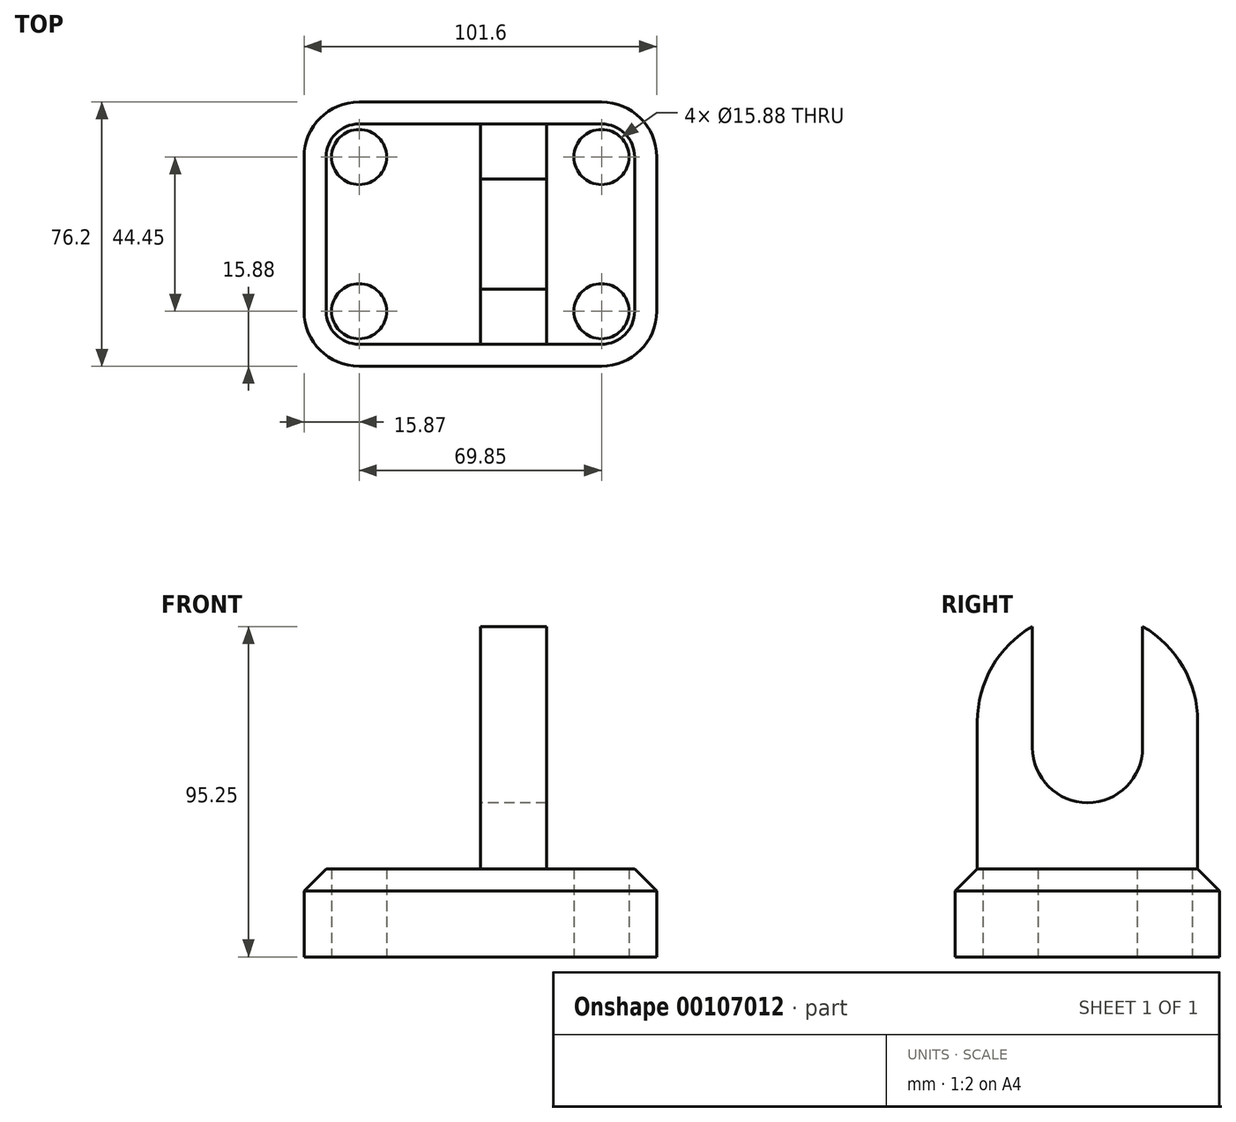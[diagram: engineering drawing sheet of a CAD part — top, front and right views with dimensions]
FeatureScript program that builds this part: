
annotation { "Feature Type Name" : "Feature", "Feature Type Description" : "" }
export const myFeature = defineFeature(function(context is Context, id is Id, definition is map)
    precondition{}
    {
        {
            var Q0;
            Q0=qCreatedBy(makeId("Top.planeOp"),FACE);
            var sketch = newSketch(context, id + "F0", { "sketchPlane" : qUnion([Q0])});
            skLineSegment(sketch, "E0.bottom", {"start": v(-44.56, 20.5) * mm, "end": v(57.04, 20.5) * mm});
            skLineSegment(sketch, "E0.top", {"start": v(-44.56, -55.7) * mm, "end": v(57.04, -55.7) * mm});
            skLineSegment(sketch, "E0.left", {"start": v(-44.56, 20.5) * mm, "end": v(-44.56, -55.7) * mm});
            skLineSegment(sketch, "E0.right", {"start": v(57.04, 20.5) * mm, "end": v(57.04, -55.7) * mm});
            skSolve(sketch);
        }
        {
            var Q0;
            Q0=makeQuery(id+"F0.imprint","IMPRINT",FACE,{"disambiguationData":[TD([[makeQuery(id+"F0.imprint","IMPRINT",EDGE,{"derivedFrom":sQuery(id+"F0.wireOp",EDGE,"E0.bottom")}),-1.0]])]});
            extrude(context, id + "F1", {"entities" : qUnion([Q0]), "depth" : 25.4 * mm});
        }
        {
            var Q0;
            Q0=makeQuery(id+"F1.opExtrude","SWEPT_EDGE",EDGE,{"disambiguationData":[OSD([sQuery(id+"F0.wireOp",EDGE,"E0.top"),sQuery(id+"F0.wireOp",EDGE,"E0.right")])]});
            fillet(context, id + "F2", {"entities" : qUnion([Q0]), "radius" : 15.88 * mm, "tangentPropagation" : true, "allowEdgeOverflow" : false});
        }
        {
            var Q0;
            Q0=makeQuery(id+"F1.opExtrude","SWEPT_EDGE",EDGE,{"disambiguationData":[OSD([sQuery(id+"F0.wireOp",EDGE,"E0.top"),sQuery(id+"F0.wireOp",EDGE,"E0.left")])]});
            fillet(context, id + "F3", {"entities" : qUnion([Q0]), "radius" : 15.88 * mm, "tangentPropagation" : true, "allowEdgeOverflow" : false});
        }
        {
            var Q0;
            Q0=makeQuery(id+"F1.opExtrude","SWEPT_EDGE",EDGE,{"disambiguationData":[OSD([sQuery(id+"F0.wireOp",EDGE,"E0.bottom"),sQuery(id+"F0.wireOp",EDGE,"E0.left")])]});
            fillet(context, id + "F4", {"entities" : qUnion([Q0]), "radius" : 15.88 * mm, "tangentPropagation" : true, "allowEdgeOverflow" : false});
        }
        {
            var Q0;
            Q0=makeQuery(id+"F1.opExtrude","SWEPT_EDGE",EDGE,{"disambiguationData":[OSD([sQuery(id+"F0.wireOp",EDGE,"E0.bottom"),sQuery(id+"F0.wireOp",EDGE,"E0.right")])]});
            fillet(context, id + "F5", {"entities" : qUnion([Q0]), "radius" : 15.88 * mm, "tangentPropagation" : true, "allowEdgeOverflow" : false});
        }
        {
            var Q0;
            Q0=makeQuery(id+"F1.opExtrude","CAP_FACE",FACE,{"disambiguationData":[OSD([sQuery(id+"F0.wireOp",EDGE,"E0.bottom"),sQuery(id+"F0.wireOp",EDGE,"E0.top"),sQuery(id+"F0.wireOp",EDGE,"E0.left"),sQuery(id+"F0.wireOp",EDGE,"E0.right")])],"isStart":true});
            var sketch = newSketch(context, id + "F6", { "sketchPlane" : qUnion([Q0])});
            skLineSegment(sketch, "E1.bottom", {"start": v(-44.56, -4.62) * mm, "end": v(-28.69, -4.62) * mm});
            skLineSegment(sketch, "E1.top", {"start": v(-44.56, -20.5) * mm, "end": v(-28.69, -20.5) * mm});
            skLineSegment(sketch, "E1.left", {"start": v(-44.56, -4.62) * mm, "end": v(-44.56, -20.5) * mm});
            skLineSegment(sketch, "E1.right", {"start": v(-28.69, -4.62) * mm, "end": v(-28.69, -20.5) * mm});
            skLineSegment(sketch, "E2.bottom", {"start": v(-44.56, 39.83) * mm, "end": v(-28.69, 39.83) * mm});
            skLineSegment(sketch, "E2.top", {"start": v(-44.56, 55.7) * mm, "end": v(-28.69, 55.7) * mm});
            skLineSegment(sketch, "E2.left", {"start": v(-44.56, 39.83) * mm, "end": v(-44.56, 55.7) * mm});
            skLineSegment(sketch, "E2.right", {"start": v(-28.69, 39.83) * mm, "end": v(-28.69, 55.7) * mm});
            skLineSegment(sketch, "E3.bottom", {"start": v(41.16, 55.7) * mm, "end": v(57.04, 55.7) * mm});
            skLineSegment(sketch, "E3.top", {"start": v(41.16, 39.83) * mm, "end": v(57.04, 39.83) * mm});
            skLineSegment(sketch, "E3.left", {"start": v(41.16, 55.7) * mm, "end": v(41.16, 39.83) * mm});
            skLineSegment(sketch, "E3.right", {"start": v(57.04, 55.7) * mm, "end": v(57.04, 39.83) * mm});
            skLineSegment(sketch, "E4.bottom", {"start": v(57.04, -4.62) * mm, "end": v(41.16, -4.62) * mm});
            skLineSegment(sketch, "E4.top", {"start": v(57.04, -20.5) * mm, "end": v(41.16, -20.5) * mm});
            skLineSegment(sketch, "E4.left", {"start": v(57.04, -4.62) * mm, "end": v(57.04, -20.5) * mm});
            skLineSegment(sketch, "E4.right", {"start": v(41.16, -4.62) * mm, "end": v(41.16, -20.5) * mm});
            skSolve(sketch);
        }
        {
            var Q0;
            Q0=sQuery(id+"F6.wireOp",VERTEX,"E2.bottom.end");
            var Q1;
            Q1=sQuery(id+"F6.wireOp",VERTEX,"E3.top.start");
            var Q2;
            Q2=sQuery(id+"F6.wireOp",VERTEX,"E4.bottom.end");
            var Q3;
            Q3=sQuery(id+"F6.wireOp",VERTEX,"E1.right.start");
            var Q4;
            Q4=makeQuery(id+"F1.opExtrude","SWEPT_BODY",BODY,{"disambiguationData":[OSD([sQuery(id+"F0.wireOp",EDGE,"E0.bottom"),sQuery(id+"F0.wireOp",EDGE,"E0.top"),sQuery(id+"F0.wireOp",EDGE,"E0.left"),sQuery(id+"F0.wireOp",EDGE,"E0.right")])]});
            hole(context, id + "F7", {"style" : HoleStyle.SIMPLE, "endStyle" : HoleEndStyle.THROUGH, "holeDiameter" : 15.88 * mm, "startFromSketch" : true, "locations" : qUnion([Q0, Q1, Q2, Q3]), "scope" : qUnion([Q4]), "isTappedThrough" : true});
        }
        {
            var Q0;
            Q0=makeQuery(id+"F1.opExtrude","CAP_EDGE",EDGE,{"disambiguationData":[OSD([sQuery(id+"F0.wireOp",EDGE,"E0.top")])],"isStart":false});
            chamfer(context, id + "F8", {"entities" : qUnion([Q0]), "width" : 6.35 * mm, "tangentPropagation" : true});
        }
        {
            var Q0;
            Q0=makeQuery(id+"F1.opExtrude","CAP_FACE",FACE,{"disambiguationData":[OSD([sQuery(id+"F0.wireOp",EDGE,"E0.bottom"),sQuery(id+"F0.wireOp",EDGE,"E0.top"),sQuery(id+"F0.wireOp",EDGE,"E0.left"),sQuery(id+"F0.wireOp",EDGE,"E0.right")])],"isStart":false});
            var sketch = newSketch(context, id + "F9", { "sketchPlane" : qUnion([Q0])});
            skLineSegment(sketch, "E5.bottom", {"start": v(6.24, -49.36) * mm, "end": v(25.29, -49.36) * mm});
            skLineSegment(sketch, "E5.top", {"start": v(6.24, 14.14) * mm, "end": v(25.29, 14.14) * mm});
            skLineSegment(sketch, "E5.left", {"start": v(6.24, -49.36) * mm, "end": v(6.24, 14.14) * mm});
            skLineSegment(sketch, "E5.right", {"start": v(25.29, -49.36) * mm, "end": v(25.29, 14.14) * mm});
            skSolve(sketch);
        }
        {
            var Q0;
            Q0=makeQuery(id+"F9.imprint","IMPRINT",FACE,{"disambiguationData":[TD([[makeQuery(id+"F9.imprint","IMPRINT",EDGE,{"derivedFrom":sQuery(id+"F9.wireOp",EDGE,"E5.bottom")}),1.0]])]});
            extrude(context, id + "F10", {"entities" : qUnion([Q0]), "operationType" : NewBodyOperationType.ADD, "depth" : 69.85 * mm});
        }
        {
            var Q0;
            Q0=makeQuery(id+"F10.opExtrude","SWEPT_FACE",FACE,{"disambiguationData":[OSD([sQuery(id+"F9.wireOp",EDGE,"E5.left")])]});
            var sketch = newSketch(context, id + "F11", { "sketchPlane" : qUnion([Q0])});
            skCircle(sketch, "E6", {"center": v(17.6, 60.33) * mm, "radius": 15.88 * mm});
            skPoint(sketch, "E7.orphan", {"position": v(-14.14, 95.25) * mm});
            skPoint(sketch, "E8.orphan", {"position": v(49.36, 25.4) * mm});
            skLineSegment(sketch, "E9", {"start": v(33.48, 60.33) * mm, "end": v(33.48, 95.25) * mm});
            skLineSegment(sketch, "E10", {"start": v(1.73, 60.33) * mm, "end": v(1.73, 95.25) * mm});
            skPoint(sketch, "E11.orphan", {"position": v(-14.14, 60.33) * mm});
            skPoint(sketch, "E12.orphan", {"position": v(49.36, 60.33) * mm});
            skSolve(sketch);
        }
        {
            var Q0;
            Q0=qSketchRegion(id+"F11",true);
            var Q1;
            {var subQ0=sQuery(id+"F11.wireOp",EDGE,"E9");Q1=makeQuery(id+"F11.imprint","IMPRINT",FACE,{"disambiguationData":[TD([[makeQuery(id+"F11.imprint","IMPRINT",EDGE,{"derivedFrom":subQ0}),1.0]])]});}
            extrude(context, id + "F12", {"entities" : qUnion([Q0, Q1]), "operationType" : NewBodyOperationType.REMOVE, "oppositeDirection" : true, "depth" : 25.4 * mm});
        }
        {
            var Q0;
            Q0=makeQuery(id+"F10.opExtrude","CAP_EDGE",EDGE,{"disambiguationData":[OSD([sQuery(id+"F9.wireOp",EDGE,"E5.bottom")])],"isStart":false});
            fillet(context, id + "F13", {"entities" : qUnion([Q0]), "radius" : 31.75 * mm, "tangentPropagation" : true, "allowEdgeOverflow" : false});
        }
        {
            var Q0;
            Q0=makeQuery(id+"F10.opExtrude","CAP_EDGE",EDGE,{"disambiguationData":[OSD([sQuery(id+"F9.wireOp",EDGE,"E5.top")])],"isStart":false});
            fillet(context, id + "F14", {"entities" : qUnion([Q0]), "radius" : 31.75 * mm, "tangentPropagation" : true, "allowEdgeOverflow" : false});
        }
    });
